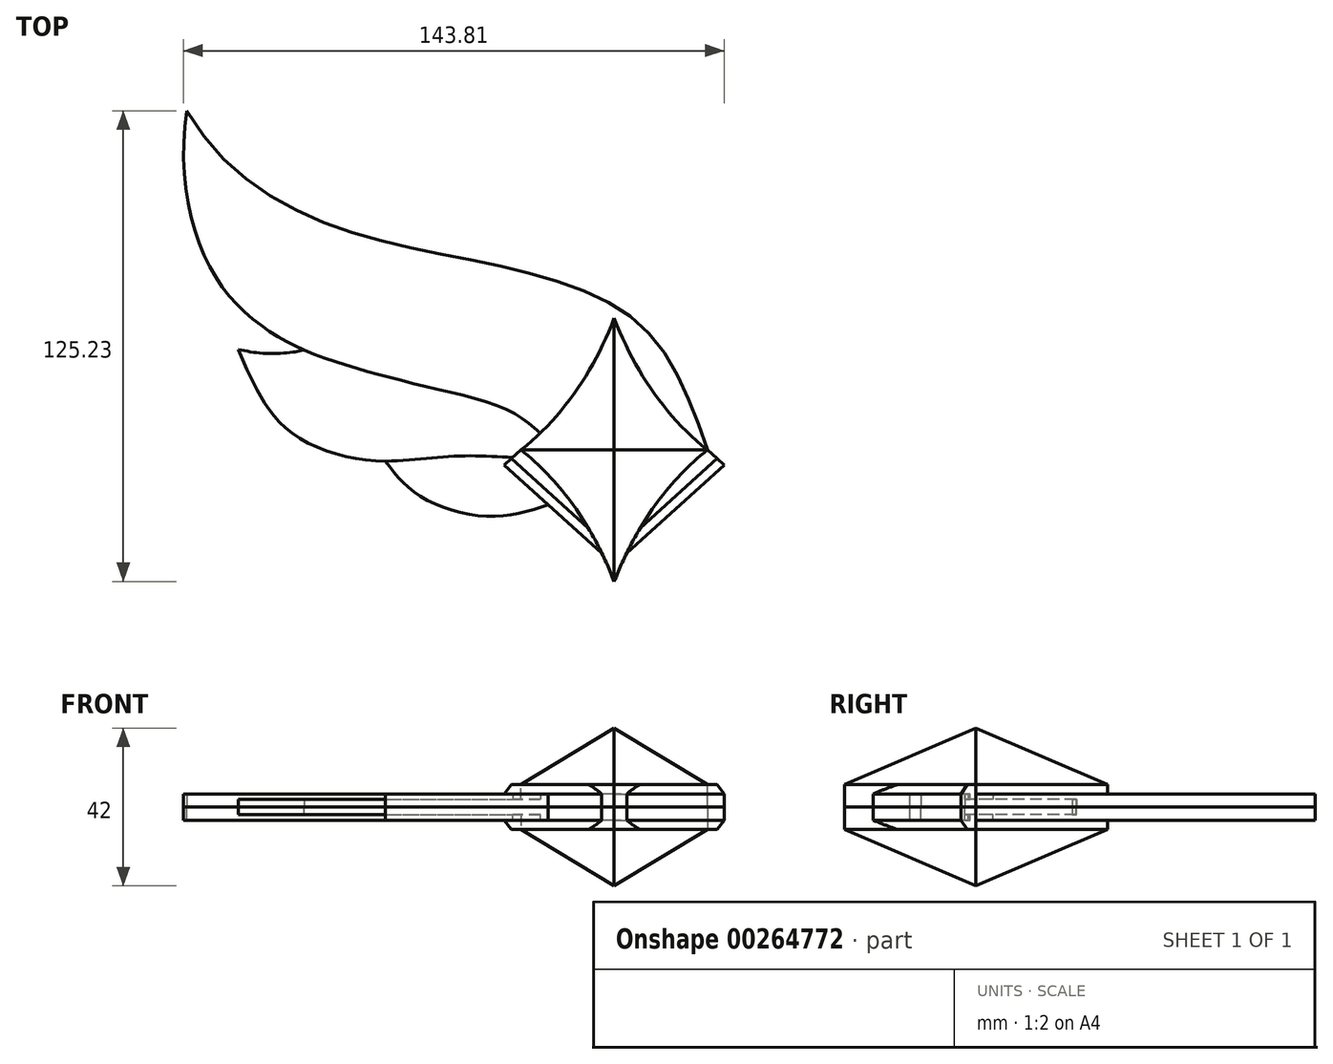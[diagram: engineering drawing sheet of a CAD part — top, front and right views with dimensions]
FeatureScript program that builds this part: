
annotation { "Feature Type Name" : "Feature", "Feature Type Description" : "" }
export const myFeature = defineFeature(function(context is Context, id is Id, definition is map)
    precondition{}
    {
        {
            var Q0;
            Q0=qCreatedBy(makeId("Top.planeOp"),FACE);
            var sketch = newSketch(context, id + "F0", { "sketchPlane" : qUnion([Q0])});
            skLineSegment(sketch, "E0", {"start": v(0, 55.19) * mm, "end": v(0, -54.81) * mm, "construction": true});
            skSolve(sketch);
        }
        {
            var Q0;
            Q0=qCreatedBy(makeId("Top.planeOp"),FACE);
            var sketch = newSketch(context, id + "F1", { "sketchPlane" : qUnion([Q0])});
            skFitSpline(sketch, "E1", {"points": [v(0, 35) * mm, v(-24.82, 0) * mm], "startDerivative": vector(-16.19, -41.46) * mm, "endDerivative": vector(-33.95, -26.9) * mm});
            skFitSpline(sketch, "E2.MirrorCS", {"points": [v(0, -35) * mm, v(-24.82, 0) * mm], "startDerivative": vector(-16.19, 41.46) * mm, "endDerivative": vector(-33.95, 26.9) * mm});
            skFitSpline(sketch, "E3.MirrorCS", {"points": [v(0, 35) * mm, v(24.82, 0) * mm], "startDerivative": vector(16.19, -41.46) * mm, "endDerivative": vector(33.95, -26.9) * mm});
            skFitSpline(sketch, "E4.MirrorCS", {"points": [v(0, -35) * mm, v(24.82, 0) * mm], "startDerivative": vector(16.19, 41.46) * mm, "endDerivative": vector(33.95, 26.9) * mm});
            skLineSegment(sketch, "E5", {"start": v(0, 35) * mm, "end": v(0, -35) * mm, "construction": true});
            skSolve(sketch);
        }
        {
            var Q0;
            Q0=qCreatedBy(makeId("Top.planeOp"),FACE);
            cPlane(context, id + "F2", {"entities" : qUnion([Q0]), "cplaneType" : CPlaneType.OFFSET, "offset" : 15 * mm, "width" : 150 * mm, "height" : 150 * mm});
        }
        {
            var Q0;
            Q0=qCreatedBy(id+"F2.planeOp",FACE);
            var sketch = newSketch(context, id + "F3", { "sketchPlane" : qUnion([Q0])});
            skPoint(sketch, "E6", {"position": v(0, 0) * mm});
            skSolve(sketch);
        }
        {
            var Q0;
            Q0=makeQuery(id+"F1.imprint","IMPRINT",FACE,{"disambiguationData":[TD([[makeQuery(id+"F1.imprint","IMPRINT",EDGE,{"derivedFrom":sQuery(id+"F1.wireOp",EDGE,"E1")}),1.0]])]});
            var Q1;
            Q1=sQuery(id+"F3.wireOp",VERTEX,"E6");
            loft(context, id + "F4", {"sheetProfilesArray" : [{ "sheetProfileEntities" : qUnion([Q0]) }, { "sheetProfileEntities" : qUnion([Q1]) }]});
        }
        {
            var Q0;
            Q0=makeQuery(id+"F4.opLoft","CAP_FACE",FACE,{"disambiguationData":[OSD([makeQuery(id+"F1.imprint","IMPRINT",FACE,{"disambiguationData":[TD([[makeQuery(id+"F1.imprint","IMPRINT",EDGE,{"derivedFrom":sQuery(id+"F1.wireOp",EDGE,"E1")}),1.0]])]})])],"isStart":true});
            var sketch = newSketch(context, id + "F5", { "sketchPlane" : qUnion([Q0])});
            skLineSegment(sketch, "E7", {"start": v(-24.82, 0) * mm, "end": v(-29.23, 4) * mm});
            skLineSegment(sketch, "E8", {"start": v(-29.23, 4) * mm, "end": v(-3.33, 27.4) * mm});
            skLineSegment(sketch, "E9.MirrorCS", {"start": v(24.82, 0) * mm, "end": v(29.23, 4) * mm});
            skLineSegment(sketch, "E10.MirrorCS", {"start": v(29.23, 4) * mm, "end": v(3.33, 27.4) * mm});
            skSolve(sketch);
        }
        {
            var Q0;
            Q0=qSketchRegion(id+"F5",true);
            var Q1;
            {var subQ0=sQuery(id+"F5.wireOp",EDGE,"E7");Q1=makeQuery(id+"F5.imprint","IMPRINT",FACE,{"disambiguationData":[TD([[makeQuery(id+"F5.imprint","IMPRINT",EDGE,{"derivedFrom":subQ0}),-1.0]])]});}
            var Q2;
            {var subQ0=sQuery(id+"F5.wireOp",EDGE,"E9.MirrorCS");Q2=makeQuery(id+"F5.imprint","IMPRINT",FACE,{"disambiguationData":[TD([[makeQuery(id+"F5.imprint","IMPRINT",EDGE,{"derivedFrom":subQ0}),1.0]])]});}
            var Q3;
            {var subQ1=sQuery(id+"F1.wireOp",EDGE,"E2.MirrorCS");var subQ2=sQuery(id+"F1.wireOp",EDGE,"E1");var subQ4=sQuery(id+"F1.wireOp",EDGE,"E3.MirrorCS");var subQ5=makeQuery(id+"F4.opLoft","MID_CAP_EDGE",EDGE,{"disambiguationData":[OSD([subQ2,subQ1,subQ4])],"capPos":0.0});Q3=makeQuery(id+"F5.imprint","IMPRINT",FACE,{"disambiguationData":[TD([[makeQuery(id+"F5.imprint","IMPRINT",EDGE,{"derivedFrom":subQ5}),-1.0]])]});}
            extrude(context, id + "F6", {"entities" : qUnion([Q0, Q1, Q2, Q3]), "operationType" : NewBodyOperationType.ADD, "depth" : 6 * mm, "offsetDistance" : 25 * mm});
        }
        {
            var Q0;
            Q0=makeQuery(id+"F6.opExtrude","CAP_EDGE",EDGE,{"disambiguationData":[OSD([sQuery(id+"F5.wireOp",EDGE,"E8")])],"isStart":true});
            var Q1;
            Q1=makeQuery(id+"F6.opExtrude","CAP_EDGE",EDGE,{"disambiguationData":[OSD([sQuery(id+"F5.wireOp",EDGE,"E10.MirrorCS")])],"isStart":true});
            chamfer(context, id + "F7", {"entities" : qUnion([Q0, Q1]), "width" : 2.5 * mm, "tangentPropagation" : true});
        }
        {
            var Q0;
            Q0=makeQuery(id+"F6.opExtrude","CAP_FACE",FACE,{"disambiguationData":[OSD([sQuery(id+"F1.wireOp",EDGE,"E1"),sQuery(id+"F1.wireOp",EDGE,"E2.MirrorCS"),sQuery(id+"F1.wireOp",EDGE,"E3.MirrorCS"),sQuery(id+"F1.wireOp",EDGE,"E4.MirrorCS"),sQuery(id+"F5.wireOp",EDGE,"E7"),sQuery(id+"F5.wireOp",EDGE,"E8"),sQuery(id+"F5.wireOp",EDGE,"E9.MirrorCS"),sQuery(id+"F5.wireOp",EDGE,"E10.MirrorCS")])],"isStart":false});
            var sketch = newSketch(context, id + "F8", { "sketchPlane" : qUnion([Q0])});
            skFitSpline(sketch, "E11", {"points": [v(24.82, 0) * mm, v(7.87, -32.42) * mm, v(-29.1, -48.58) * mm, v(-77.19, -60.45) * mm, v(-113.78, -90.23) * mm], "startDerivative": vector(-55.4, -157.68) * mm, "endDerivative": vector(-96.06, -166.48) * mm});
            skFitSpline(sketch, "E12", {"points": [v(-113.78, -90.23) * mm, v(-106.77, -47.21) * mm, v(-88.67, -29.7) * mm, v(-70.57, -22.3) * mm, v(-49.94, -16.85) * mm, v(-28.33, -10.62) * mm, v(-19.68, -4.5) * mm], "startDerivative": vector(-31, 215.6) * mm, "endDerivative": vector(64.01, 57.07) * mm});
            skFitSpline(sketch, "E13", {"points": [v(-82.53, -26.61) * mm, v(-85.09, -26.05) * mm, v(-92.8, -25.64) * mm, v(-99.95, -26.74) * mm], "startDerivative": vector(-9.5, 2.74) * mm, "endDerivative": vector(-17.94, -3.83) * mm});
            skFitSpline(sketch, "E14", {"points": [v(-99.95, -26.74) * mm, v(-94.72, -15.32) * mm, v(-85.09, -4.03) * mm, v(-64.44, 2.85) * mm, v(-44.2, 1.75) * mm, v(-27.02, 2) * mm], "startDerivative": vector(27.56, 67.04) * mm, "endDerivative": vector(84.57, 4.76) * mm});
            skFitSpline(sketch, "E15", {"points": [v(-60.87, 2.99) * mm, v(-51.78, 12.2) * mm, v(-33.2, 17.71) * mm, v(-17.53, 14.57) * mm], "startDerivative": vector(24.78, 34.37) * mm, "endDerivative": vector(44.8, -14.57) * mm});
            skSolve(sketch);
        }
        {
            var Q0;
            {var subQ7=sQuery(id+"F8.wireOp",EDGE,"E11");Q0=makeQuery(id+"F8.imprint","IMPRINT",FACE,{"disambiguationData":[TD([[makeQuery(id+"F8.imprint","IMPRINT",EDGE,{"derivedFrom":subQ7}),-1.0]])]});}
            var Q1;
            {var subQ3=sQuery(id+"F8.wireOp",EDGE,"E15");Q1=makeQuery(id+"F8.imprint","IMPRINT",FACE,{"disambiguationData":[TD([[makeQuery(id+"F8.imprint","IMPRINT",EDGE,{"derivedFrom":subQ3}),-1.0]])]});}
            extrude(context, id + "F9", {"entities" : qUnion([Q0, Q1]), "operationType" : NewBodyOperationType.ADD, "oppositeDirection" : true, "depth" : 3.5 * mm, "offsetDistance" : 25 * mm});
        }
        {
            var Q0;
            {var subQ4=sQuery(id+"F8.wireOp",EDGE,"E13");Q0=makeQuery(id+"F8.imprint","IMPRINT",FACE,{"disambiguationData":[TD([[makeQuery(id+"F8.imprint","IMPRINT",EDGE,{"derivedFrom":subQ4}),-1.0]])]});}
            extrude(context, id + "F10", {"entities" : qUnion([Q0]), "operationType" : NewBodyOperationType.ADD, "oppositeDirection" : true, "depth" : 2 * mm, "offsetDistance" : 25 * mm});
        }
        {
            var Q0;
            Q0=makeQuery(id+"F4.opLoft","SWEPT_BODY",BODY,{"disambiguationData":[OSD([makeQuery(id+"F1.imprint","IMPRINT",FACE,{"disambiguationData":[TD([[makeQuery(id+"F1.imprint","IMPRINT",EDGE,{"derivedFrom":sQuery(id+"F1.wireOp",EDGE,"E1")}),1.0]])]}),sQuery(id+"F3.wireOp",VERTEX,"E6")])]});
            var Q1;
            Q1=makeQuery(id+"F8.imprint","IMPRINT",FACE,{"disambiguationData":[TD([[makeQuery(id+"F8.imprint","IMPRINT",EDGE,{"derivedFrom":makeQuery(id+"F6.opExtrude","CAP_EDGE",EDGE,{"disambiguationData":[OSD([sQuery(id+"F5.wireOp",EDGE,"E9.MirrorCS")])],"isStart":false})}),1.0]])]});
            mirror(context, id + "F11", {"entities" : qUnion([Q0]), "mirrorPlane" : qUnion([Q1])});
        }
    });
